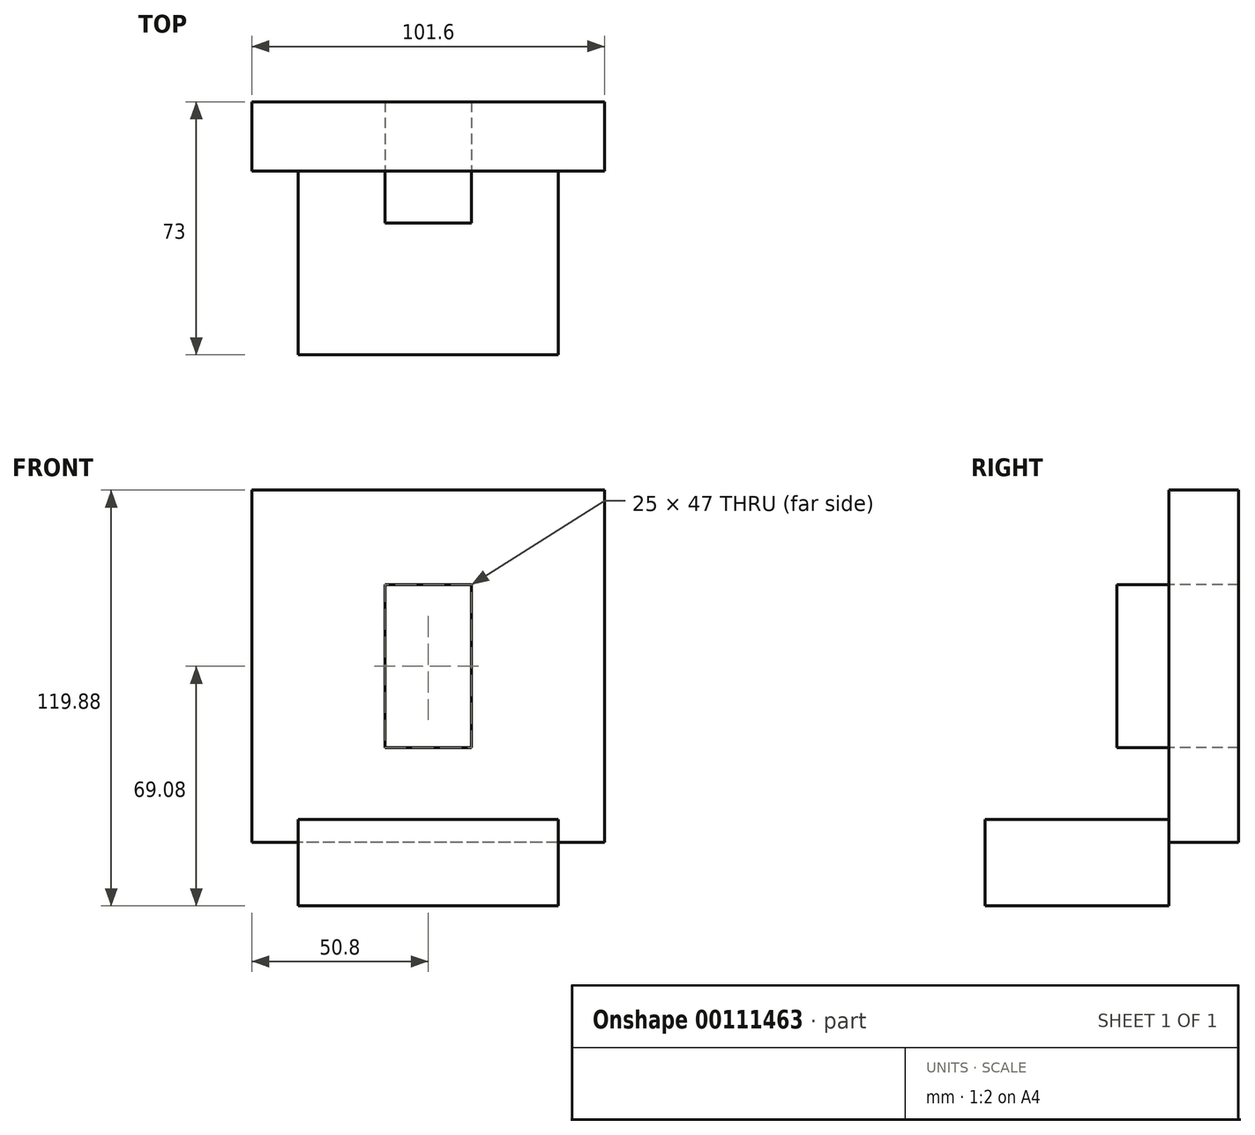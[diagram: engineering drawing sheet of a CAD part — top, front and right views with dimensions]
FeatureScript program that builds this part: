
annotation { "Feature Type Name" : "Feature", "Feature Type Description" : "" }
export const myFeature = defineFeature(function(context is Context, id is Id, definition is map)
    precondition{}
    {
        {
            var Q0;
            Q0=qCreatedBy(makeId("Front.planeOp"),FACE);
            var sketch = newSketch(context, id + "F0", { "sketchPlane" : qUnion([Q0])});
            skLineSegment(sketch, "E0.bottom", {"start": v(50.8, -50.8) * mm, "end": v(-50.8, -50.8) * mm});
            skLineSegment(sketch, "E0.top", {"start": v(50.8, 50.8) * mm, "end": v(-50.8, 50.8) * mm});
            skLineSegment(sketch, "E0.left", {"start": v(50.8, -50.8) * mm, "end": v(50.8, 50.8) * mm});
            skLineSegment(sketch, "E0.right", {"start": v(-50.8, -50.8) * mm, "end": v(-50.8, 50.8) * mm});
            skPoint(sketch, "E0.middle", {"position": v(0, 0) * mm});
            skLineSegment(sketch, "E1.bottom", {"start": v(12.5, 23.5) * mm, "end": v(-12.5, 23.5) * mm});
            skLineSegment(sketch, "E1.top", {"start": v(12.5, -23.5) * mm, "end": v(-12.5, -23.5) * mm});
            skLineSegment(sketch, "E1.left", {"start": v(12.5, 23.5) * mm, "end": v(12.5, -23.5) * mm});
            skLineSegment(sketch, "E1.right", {"start": v(-12.5, 23.5) * mm, "end": v(-12.5, -23.5) * mm});
            skSolve(sketch);
        }
        {
            var Q0;
            Q0=makeQuery(id+"F0.imprint","IMPRINT",FACE,{"disambiguationData":[TD([[makeQuery(id+"F0.imprint","IMPRINT",EDGE,{"derivedFrom":sQuery(id+"F0.wireOp",EDGE,"E1.bottom")}),1.0]])]});
            extrude(context, id + "F1", {"entities" : qUnion([Q0]), "depth" : 15 * mm});
        }
        {
            var Q0;
            Q0=makeQuery(id+"F0.imprint","IMPRINT",FACE,{"disambiguationData":[TD([[makeQuery(id+"F0.imprint","IMPRINT",EDGE,{"derivedFrom":sQuery(id+"F0.wireOp",EDGE,"E0.bottom")}),-1.0]])]});
            extrude(context, id + "F2", {"entities" : qUnion([Q0]), "oppositeDirection" : true, "depth" : 20 * mm});
        }
        {
            var Q0;
            Q0=qCreatedBy(makeId("Front.planeOp"),FACE);
            var sketch = newSketch(context, id + "F3", { "sketchPlane" : qUnion([Q0])});
            skLineSegment(sketch, "E2.bottom", {"start": v(37.5, -69.08) * mm, "end": v(-37.5, -69.08) * mm});
            skLineSegment(sketch, "E2.top", {"start": v(37.5, -44.08) * mm, "end": v(-37.5, -44.08) * mm});
            skLineSegment(sketch, "E2.left", {"start": v(37.5, -69.08) * mm, "end": v(37.5, -44.08) * mm});
            skLineSegment(sketch, "E2.right", {"start": v(-37.5, -69.08) * mm, "end": v(-37.5, -44.08) * mm});
            skPoint(sketch, "E2.middle", {"position": v(0, -56.58) * mm});
            skSolve(sketch);
        }
        {
            var Q0;
            Q0=makeQuery(id+"F3.imprint","IMPRINT",FACE,{"disambiguationData":[TD([[makeQuery(id+"F3.imprint","IMPRINT",EDGE,{"derivedFrom":sQuery(id+"F3.wireOp",EDGE,"E2.bottom")}),-1.0]])]});
            extrude(context, id + "F4", {"entities" : qUnion([Q0]), "operationType" : NewBodyOperationType.ADD, "depth" : 53 * mm});
        }
    });
